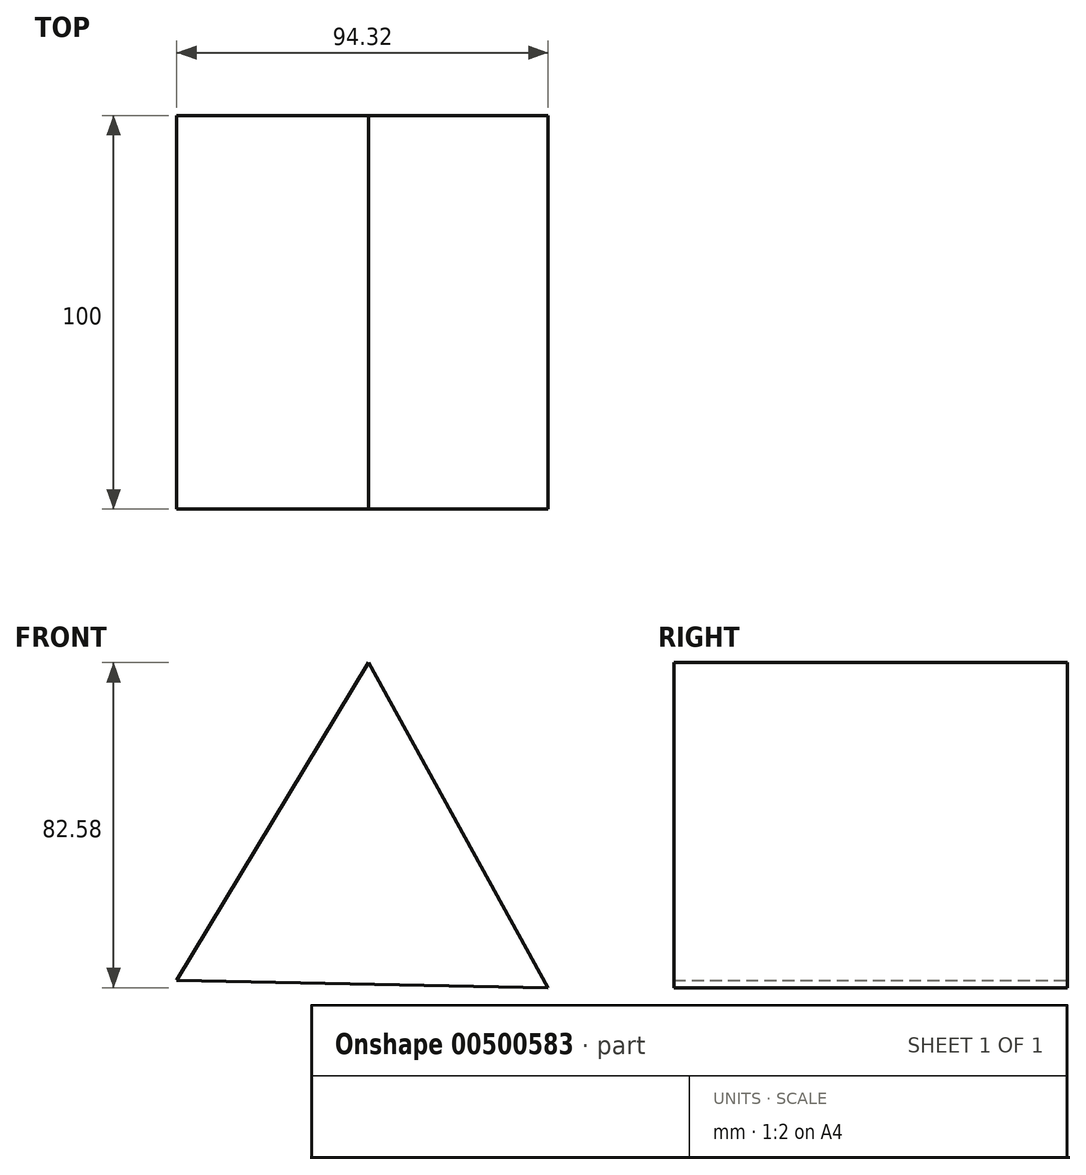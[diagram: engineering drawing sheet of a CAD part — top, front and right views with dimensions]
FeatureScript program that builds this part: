
annotation { "Feature Type Name" : "Feature", "Feature Type Description" : "" }
export const myFeature = defineFeature(function(context is Context, id is Id, definition is map)
    precondition{}
    {
        {
            var Q0;
            Q0=qCreatedBy(makeId("Front.planeOp"),FACE);
            var sketch = newSketch(context, id + "F0", { "sketchPlane" : qUnion([Q0])});
            skCircle(sketch, "E0.cCircle", {"center": v(0, 0) * mm, "radius": 54.46 * mm, "construction": true});
            skLineSegment(sketch, "E0.0", {"start": v(46.64, -28.13) * mm, "end": v(-47.68, -26.32) * mm});
            skLineSegment(sketch, "E0.1", {"start": v(-47.68, -26.32) * mm, "end": v(1.04, 54.45) * mm});
            skLineSegment(sketch, "E0.2", {"start": v(1.04, 54.45) * mm, "end": v(46.64, -28.13) * mm});
            skSolve(sketch);
        }
        {
            var Q0;
            Q0=makeQuery(id+"F0.imprint","IMPRINT",FACE,{"disambiguationData":[TD([[makeQuery(id+"F0.imprint","IMPRINT",EDGE,{"derivedFrom":sQuery(id+"F0.wireOp",EDGE,"E0.0")}),-1.0]])]});
            extrude(context, id + "F1", {"entities" : qUnion([Q0]), "endBound" : BoundingType.SYMMETRIC, "depth" : 100 * mm});
        }
    });
